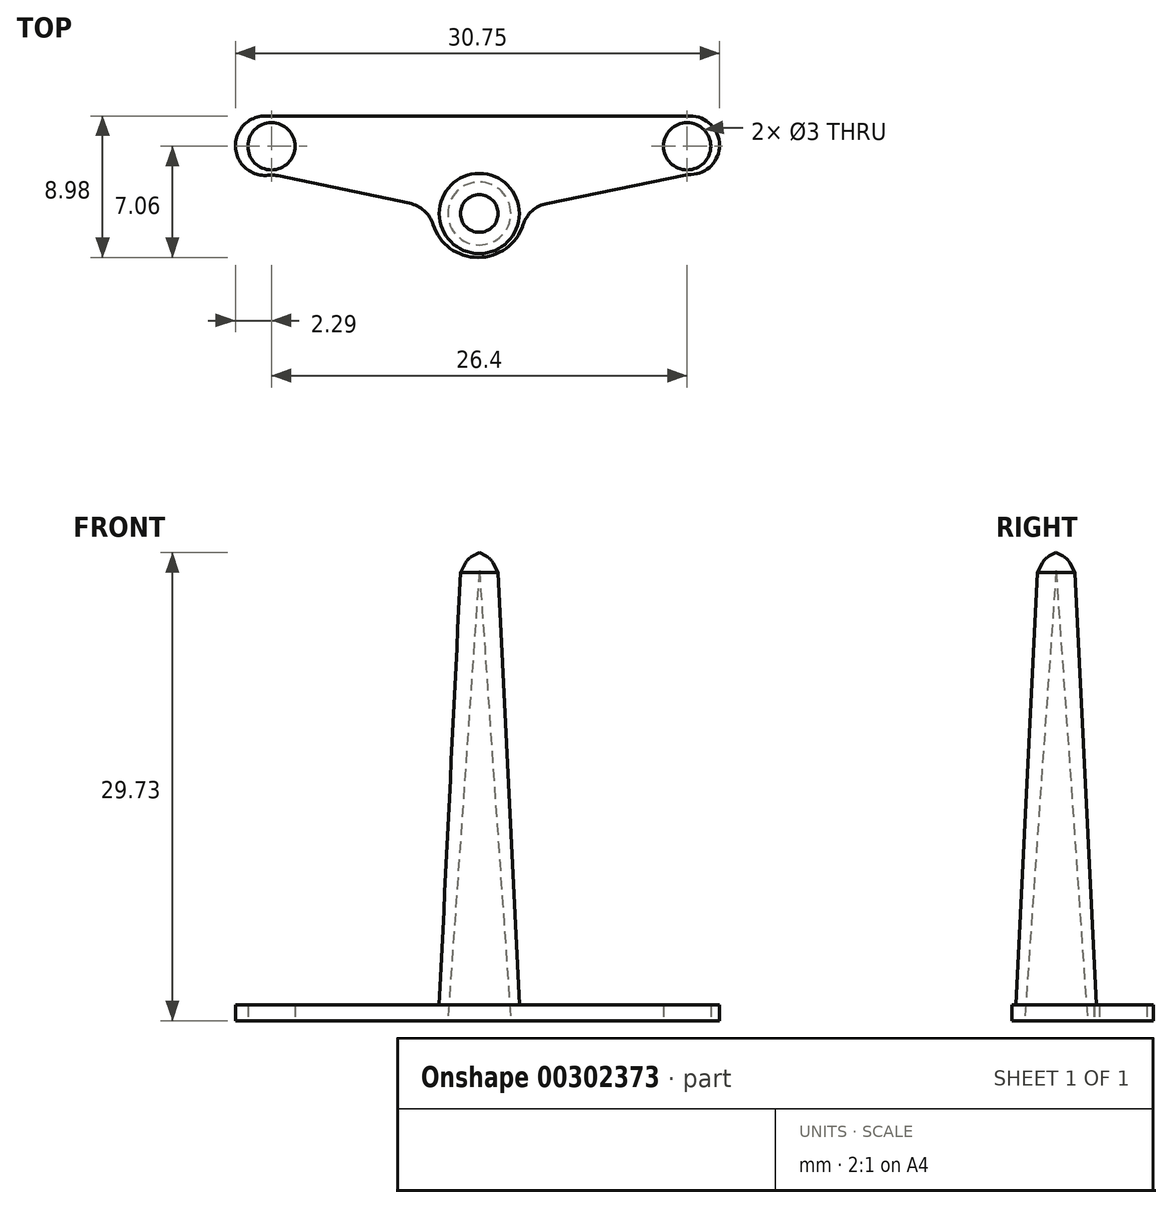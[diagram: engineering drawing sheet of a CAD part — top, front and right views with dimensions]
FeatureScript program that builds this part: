
annotation { "Feature Type Name" : "Feature", "Feature Type Description" : "" }
export const myFeature = defineFeature(function(context is Context, id is Id, definition is map)
    precondition{}
    {
        {
            var Q0;
            Q0=qCreatedBy(makeId("Top.planeOp"),FACE);
            var sketch = newSketch(context, id + "F0", { "sketchPlane" : qUnion([Q0])});
            skCircle(sketch, "E0", {"center": v(13.2, 0) * mm, "radius": 1.5 * mm});
            skCircle(sketch, "E1", {"center": v(-13.2, 0) * mm, "radius": 1.5 * mm});
            skCircle(sketch, "E2", {"center": v(0, -4.3) * mm, "radius": 2.25 * mm});
            skLineSegment(sketch, "E3", {"start": v(-13.6, 1.92) * mm, "end": v(13.4, 1.92) * mm});
            skLineSegment(sketch, "E4", {"start": v(13.3, -1.8) * mm, "end": v(2.93, -3.91) * mm});
            skLineSegment(sketch, "E5", {"start": v(-3.07, -3.9) * mm, "end": v(-13.14, -1.8) * mm});
            skArc(sketch, "E6", {"start": v(-3.07, -3.9) * mm, "mid": v(-0.07, -7.06) * mm, "end": v(2.93, -3.91) * mm});
            skArc(sketch, "E7", {"start": v(-13.6, 1.92) * mm, "mid": v(-15.48, -0.2) * mm, "end": v(-13.14, -1.8) * mm});
            skArc(sketch, "E8", {"start": v(13.3, -1.8) * mm, "mid": v(15.26, 0.01) * mm, "end": v(13.4, 1.92) * mm});
            skSolve(sketch);
        }
        {
            var Q0;
            Q0=makeQuery(id+"F0.imprint","IMPRINT",FACE,{"disambiguationData":[TD([[makeQuery(id+"F0.imprint","IMPRINT",EDGE,{"derivedFrom":sQuery(id+"F0.wireOp",EDGE,"E0")}),-1.0]])]});
            extrude(context, id + "F1", {"entities" : qUnion([Q0]), "depth" : 1 * mm});
        }
        {
            var Q0;
            Q0=makeQuery(id+"F1.opExtrude","SWEPT_EDGE",EDGE,{"disambiguationData":[OSD([sQuery(id+"F0.wireOp",EDGE,"wZEvoJSm-HYID-Hhe1-ZXtI-WF3QD8HPltNx"),sQuery(id+"F0.wireOp",EDGE,"E5")])]});
            var Q1;
            Q1=makeQuery(id+"F1.opExtrude","SWEPT_EDGE",EDGE,{"disambiguationData":[OSD([sQuery(id+"F0.wireOp",EDGE,"E4"),sQuery(id+"F0.wireOp",EDGE,"E9VXFBns-hIW4-43Tg-ypFd-AsWO8vhW3G2f")])]});
            var Q2;
            Q2=makeQuery(id+"F1.opExtrude","SWEPT_EDGE",EDGE,{"disambiguationData":[OSD([sQuery(id+"F0.wireOp",EDGE,"UwzrC3X2-5T1B-Ua9J-JAba-evbAcDEog48F"),sQuery(id+"F0.wireOp",EDGE,"IHKKSKDL-slMP-TeOy-FQml-pDefyCOIIaSv")])]});
            var Q3;
            Q3=makeQuery(id+"F1.opExtrude","SWEPT_EDGE",EDGE,{"disambiguationData":[OSD([sQuery(id+"F0.wireOp",EDGE,"E9VXFBns-hIW4-43Tg-ypFd-AsWO8vhW3G2f"),sQuery(id+"F0.wireOp",EDGE,"UwzrC3X2-5T1B-Ua9J-JAba-evbAcDEog48F")])]});
            var Q4;
            Q4=makeQuery(id+"F1.opExtrude","SWEPT_EDGE",EDGE,{"disambiguationData":[OSD([sQuery(id+"F0.wireOp",EDGE,"IHKKSKDL-slMP-TeOy-FQml-pDefyCOIIaSv"),sQuery(id+"F0.wireOp",EDGE,"wZEvoJSm-HYID-Hhe1-ZXtI-WF3QD8HPltNx")])]});
            fillet(context, id + "F2", {"entities" : qUnion([Q0, Q1, Q2, Q3, Q4]), "radius" : 2 * mm, "tangentPropagation" : true, "allowEdgeOverflow" : false});
        }
        {
            var Q0;
            Q0=qCreatedBy(makeId("Right.planeOp"),FACE);
            var sketch = newSketch(context, id + "F3", { "sketchPlane" : qUnion([Q0])});
            skLineSegment(sketch, "E9", {"start": v(-4.27, 5.73) * mm, "end": v(-4.27, 29.73) * mm, "construction": true});
            skLineSegment(sketch, "E10", {"start": v(-1.67, 0) * mm, "end": v(-3.07, 28.46) * mm});
            skLineSegment(sketch, "E11", {"start": v(-3.07, 28.46) * mm, "end": v(-3.54, 29.36) * mm});
            skLineSegment(sketch, "E12", {"start": v(-3.54, 29.36) * mm, "end": v(-4.27, 29.73) * mm});
            skLineSegment(sketch, "E13", {"start": v(-4.27, 29.73) * mm, "end": v(-4.27, 29.73) * mm});
            skLineSegment(sketch, "E14", {"start": v(-4.27, 29.73) * mm, "end": v(-4.27, 0) * mm});
            skLineSegment(sketch, "E15", {"start": v(-1.67, 0) * mm, "end": v(-4.27, 0) * mm});
            skSolve(sketch);
        }
        {
            var Q0;
            Q0=makeQuery(id+"F3.imprint","IMPRINT",FACE,{"disambiguationData":[TD([[makeQuery(id+"F3.imprint","IMPRINT",EDGE,{"derivedFrom":sQuery(id+"F3.wireOp",EDGE,"E10")}),1.0]])]});
            var Q1;
            Q1=sQuery(id+"F3.wireOp",EDGE,"E9");
            revolve(context, id + "F4", {"operationType" : NewBodyOperationType.ADD, "entities" : qUnion([Q0]), "axis" : qUnion([Q1]), "revolveType" : RevolveType.FULL});
        }
        {
            var Q0;
            Q0=makeQuery(id+"F0.imprint","IMPRINT",FACE,{"disambiguationData":[TD([[makeQuery(id+"F0.imprint","IMPRINT",EDGE,{"derivedFrom":sQuery(id+"F0.wireOp",EDGE,"E2")}),1.0]])]});
            var sketch = newSketch(context, id + "F5", { "sketchPlane" : qUnion([Q0])});
            skCircle(sketch, "E16", {"center": v(0, -4.27) * mm, "radius": 2 * mm});
            skSolve(sketch);
        }
        {
            var Q0;
            Q0 = qSketchRegion(id + "F5", true);
            extrude(context, id + "F6", {"entities" : qUnion([Q0]), "operationType" : NewBodyOperationType.REMOVE, "endBound" : BoundingType.THROUGH_ALL, "depth" : 27 * mm, "hasDraft" : true, "draftAngle" : 4 * degree, "draftPullDirection" : true});
        }
        {
            var Q0;
            Q0=makeQuery(id+"F4.opRevolve","SWEPT_EDGE",EDGE,{"disambiguationData":[OSD([sQuery(id+"F3.wireOp",EDGE,"E11"),sQuery(id+"F3.wireOp",EDGE,"E12")])]});
            fillet(context, id + "F7", {"entities" : qUnion([Q0]), "radius" : 1 * mm, "tangentPropagation" : true, "allowEdgeOverflow" : false});
        }
    });
